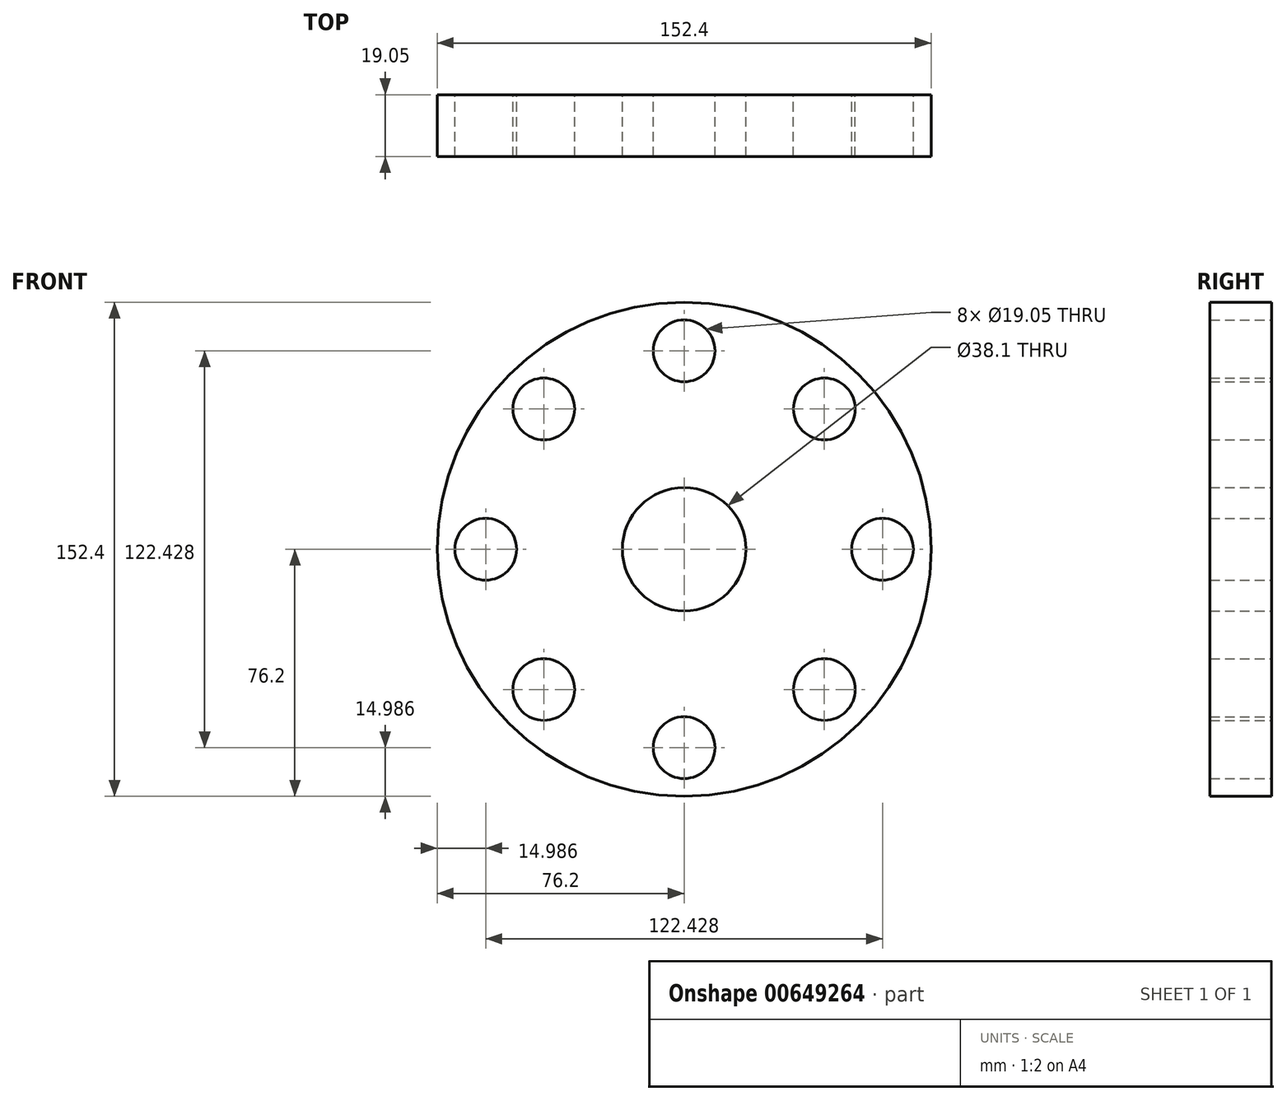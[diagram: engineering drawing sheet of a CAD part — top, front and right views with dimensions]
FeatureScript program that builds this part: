
annotation { "Feature Type Name" : "Feature", "Feature Type Description" : "" }
export const myFeature = defineFeature(function(context is Context, id is Id, definition is map)
    precondition{}
    {
        {
            var Q0;
            Q0=qCreatedBy(makeId("Front.planeOp"),FACE);
            var sketch = newSketch(context, id + "F0", { "sketchPlane" : qUnion([Q0])});
            skCircle(sketch, "E0", {"center": v(0, 0) * mm, "radius": 76.2 * mm});
            skCircle(sketch, "E1", {"center": v(0, 61.21) * mm, "radius": 9.53 * mm});
            skCircle(sketch, "E2.1.0", {"center": v(-43.28, 43.28) * mm, "radius": 9.53 * mm});
            skCircle(sketch, "E2.2.0", {"center": v(-61.21, 0) * mm, "radius": 9.53 * mm});
            skCircle(sketch, "E2.3.0", {"center": v(-43.28, -43.28) * mm, "radius": 9.53 * mm});
            skCircle(sketch, "E2.4.0", {"center": v(0, -61.21) * mm, "radius": 9.53 * mm});
            skCircle(sketch, "E2.5.0", {"center": v(43.28, -43.28) * mm, "radius": 9.53 * mm});
            skCircle(sketch, "E2.6.0", {"center": v(61.21, 0) * mm, "radius": 9.53 * mm});
            skCircle(sketch, "E2.7.0", {"center": v(43.28, 43.28) * mm, "radius": 9.53 * mm});
            skSolve(sketch);
        }
        {
            var Q0;
            Q0=makeQuery(id+"F0.imprint","IMPRINT",FACE,{"disambiguationData":[TD([[makeQuery(id+"F0.imprint","IMPRINT",EDGE,{"derivedFrom":sQuery(id+"F0.wireOp",EDGE,"E0")}),1.0]])]});
            extrude(context, id + "F1", {"entities" : qUnion([Q0]), "depth" : 19.05 * mm, "offsetDistance" : 25.4 * mm});
        }
        {
            var Q0;
            Q0=qCreatedBy(makeId("Front.planeOp"),FACE);
            var sketch = newSketch(context, id + "F2", { "sketchPlane" : qUnion([Q0])});
            skCircle(sketch, "E3", {"center": v(0, 0) * mm, "radius": 19.05 * mm});
            skSolve(sketch);
        }
        {
            var Q0;
            Q0=makeQuery(id+"F2.imprint","IMPRINT",FACE,{"disambiguationData":[TD([[makeQuery(id+"F2.imprint","IMPRINT",EDGE,{"derivedFrom":sQuery(id+"F2.wireOp",EDGE,"E3")}),1.0]])]});
            extrude(context, id + "F3", {"entities" : qUnion([Q0]), "operationType" : NewBodyOperationType.REMOVE, "depth" : 25.4 * mm, "offsetDistance" : 25.4 * mm});
        }
    });
